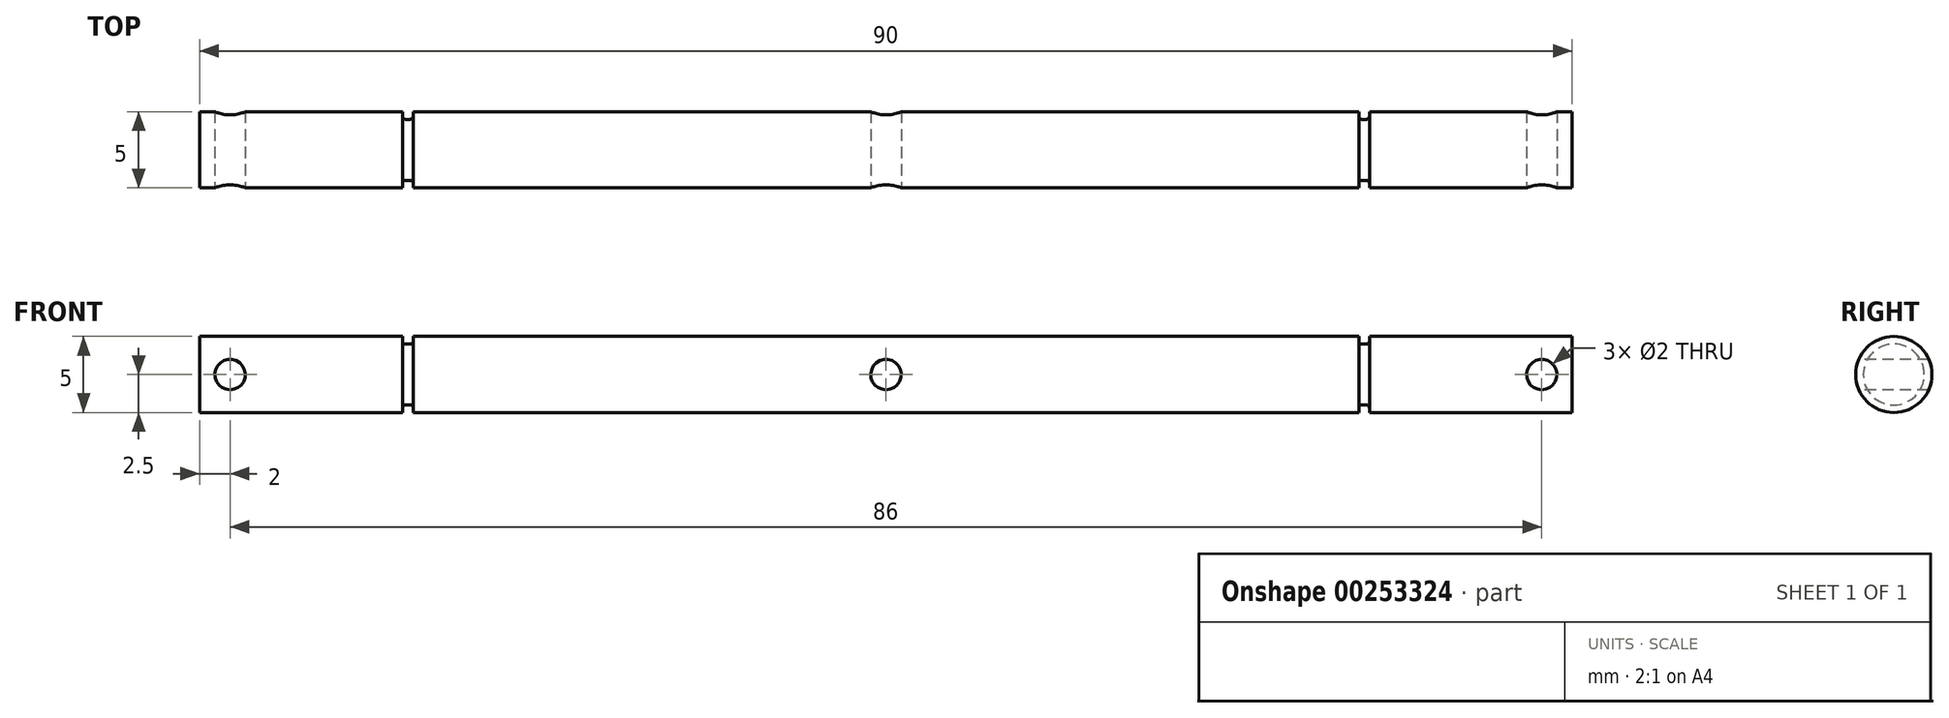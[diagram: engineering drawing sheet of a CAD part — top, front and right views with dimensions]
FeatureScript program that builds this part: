
annotation { "Feature Type Name" : "Feature", "Feature Type Description" : "" }
export const myFeature = defineFeature(function(context is Context, id is Id, definition is map)
    precondition{}
    {
        {
            var Q0;
            Q0=qCreatedBy(makeId("Front.planeOp"),FACE);
            var sketch = newSketch(context, id + "F0", { "sketchPlane" : qUnion([Q0])});
            skLineSegment(sketch, "E0.bottom", {"start": v(45, 2.5) * mm, "end": v(-45, 2.5) * mm});
            skLineSegment(sketch, "E0.top", {"start": v(45, -2.5) * mm, "end": v(-45, -2.5) * mm, "construction": true});
            skLineSegment(sketch, "E0.left", {"start": v(45, 2.5) * mm, "end": v(45, -2.5) * mm});
            skLineSegment(sketch, "E0.right", {"start": v(-45, 2.5) * mm, "end": v(-45, -2.5) * mm});
            skPoint(sketch, "E0.middle", {"position": v(0, 0) * mm});
            skCircle(sketch, "E1", {"center": v(-43, 0) * mm, "radius": 1 * mm, "construction": true});
            skCircle(sketch, "E2.MirrorC", {"center": v(43, 0) * mm, "radius": 1 * mm, "construction": true});
            skCircle(sketch, "E3", {"center": v(0, 0) * mm, "radius": 1 * mm, "construction": true});
            skLineSegment(sketch, "E4", {"start": v(-48.87, 0) * mm, "end": v(46.82, 0) * mm});
            skSolve(sketch);
        }
        {
            var Q0;
            {var subQ0=sQuery(id+"F0.wireOp",EDGE,"E0.bottom");Q0=makeQuery(id+"F0.imprint","IMPRINT",FACE,{"disambiguationData":[TD([[makeQuery(id+"F0.imprint","IMPRINT",EDGE,{"derivedFrom":subQ0}),1.0]])]});}
            var Q1;
            Q1=sQuery(id+"F0.wireOp",EDGE,"E4");
            revolve(context, id + "F1", {"entities" : qUnion([Q0]), "axis" : qUnion([Q1]), "revolveType" : RevolveType.FULL});
        }
        {
            var Q0;
            Q0=qCreatedBy(makeId("Front.planeOp"),FACE);
            var sketch = newSketch(context, id + "F2", { "sketchPlane" : qUnion([Q0])});
            skCircle(sketch, "E5.0", {"center": v(-43, 0) * mm, "radius": 1 * mm});
            skCircle(sketch, "E6.0", {"center": v(0, 0) * mm, "radius": 1 * mm});
            skCircle(sketch, "E7.0", {"center": v(43, 0) * mm, "radius": 1 * mm});
            skSolve(sketch);
        }
        {
            var Q0;
            Q0 = qSketchRegion(id + "F2", true);
            extrude(context, id + "F3", {"entities" : qUnion([Q0]), "operationType" : NewBodyOperationType.REMOVE, "endBound" : BoundingType.SYMMETRIC, "oppositeDirection" : true, "depth" : 25 * mm});
        }
        {
            var Q0;
            Q0=qCreatedBy(makeId("Front.planeOp"),FACE);
            var sketch = newSketch(context, id + "F4", { "sketchPlane" : qUnion([Q0])});
            skLineSegment(sketch, "E8", {"start": v(-31, 2) * mm, "end": v(-31, -2) * mm, "construction": true});
            skLineSegment(sketch, "E9.bottom", {"start": v(-31, 2) * mm, "end": v(-31.7, 2) * mm});
            skLineSegment(sketch, "E9.top", {"start": v(-31, 3) * mm, "end": v(-31.7, 3) * mm});
            skLineSegment(sketch, "E9.left", {"start": v(-31, 2) * mm, "end": v(-31, 3) * mm});
            skLineSegment(sketch, "E9.right", {"start": v(-31.7, 2) * mm, "end": v(-31.7, 3) * mm});
            skPoint(sketch, "E9.middle", {"position": v(-31.35, 2.5) * mm});
            skLineSegment(sketch, "E10", {"start": v(-34.7, 0) * mm, "end": v(38.79, 0) * mm, "construction": true});
            skPoint(sketch, "E10.startSnap0", {"position": v(-31, 0) * mm});
            skPoint(sketch, "E10.endSnap0", {"position": v(-31, 0) * mm});
            skLineSegment(sketch, "E11.MirrorCS", {"start": v(31, 2) * mm, "end": v(31, 3) * mm});
            skLineSegment(sketch, "E12.MirrorCS", {"start": v(31, 3) * mm, "end": v(31.7, 3) * mm});
            skLineSegment(sketch, "E13.MirrorCS", {"start": v(31.7, 2) * mm, "end": v(31.7, 3) * mm});
            skLineSegment(sketch, "E14.MirrorCS", {"start": v(31, 2) * mm, "end": v(31.7, 2) * mm});
            skSolve(sketch);
        }
        {
            var Q0;
            Q0 = qSketchRegion(id + "F4", true);
            var Q1;
            Q1=sQuery(id+"F0.wireOp",EDGE,"E4");
            revolve(context, id + "F5", {"operationType" : NewBodyOperationType.REMOVE, "entities" : qUnion([Q0]), "axis" : qUnion([Q1]), "revolveType" : RevolveType.FULL, "oppositeDirection" : true});
        }
        {
            var Q0;
            Q0=makeQuery(id+"F5.boolean.opBoolean","COPY",EDGE,{"derivedFrom":makeQuery(id+"F5.opRevolve","SWEPT_EDGE",EDGE,{"disambiguationData":[OSD([sQuery(id+"F4.wireOp",EDGE,"E9.bottom"),sQuery(id+"F4.wireOp",EDGE,"E9.right")])]})});
            var Q1;
            Q1=makeQuery(id+"F5.boolean.opBoolean","COPY",EDGE,{"derivedFrom":makeQuery(id+"F5.opRevolve","SWEPT_EDGE",EDGE,{"disambiguationData":[OSD([sQuery(id+"F4.wireOp",EDGE,"E9.bottom"),sQuery(id+"F4.wireOp",EDGE,"E9.left")])]})});
            var Q2;
            Q2=makeQuery(id+"F5.boolean.opBoolean","COPY",EDGE,{"derivedFrom":makeQuery(id+"F5.opRevolve","SWEPT_EDGE",EDGE,{"disambiguationData":[OSD([sQuery(id+"F4.wireOp",EDGE,"E13.MirrorCS"),sQuery(id+"F4.wireOp",EDGE,"E14.MirrorCS")])]})});
            var Q3;
            Q3=makeQuery(id+"F5.boolean.opBoolean","COPY",EDGE,{"derivedFrom":makeQuery(id+"F5.opRevolve","SWEPT_EDGE",EDGE,{"disambiguationData":[OSD([sQuery(id+"F4.wireOp",EDGE,"E11.MirrorCS"),sQuery(id+"F4.wireOp",EDGE,"E14.MirrorCS")])]})});
            fillet(context, id + "F6", {"entities" : qUnion([Q0, Q1, Q2, Q3]), "radius" : .2 * mm, "tangentPropagation" : true, "allowEdgeOverflow" : false});
        }
    });
